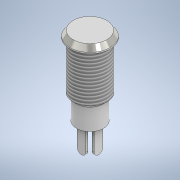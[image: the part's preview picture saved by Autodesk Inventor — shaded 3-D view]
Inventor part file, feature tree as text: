
AUTODESK INVENTOR PART (.ipt)
format: ipt  version: 2021 (Build 250183000, 183)  size: 164,864 bytes
history: native  units: mm
features: extrude x4, sketch x4, chamfer x2, thread x1, fillet x1
ambient origin geometry x8: Origin, YZ Plane, XZ Plane, XY Plane, X Axis, Y Axis, Z Axis, Center Point
bodies: Solid1 (feature_tree)
feature tree (12):
  extrude  "Extrusion1"  Depth=1.5mm TaperAngle=0.0deg
  chamfer  "Chamfer1"  Distance=0.8mm Angle=60.0deg
  extrude  "Extrusion2"  Depth=12.0mm TaperAngle=0.0deg
  chamfer  "Chamfer2"  Distance=0.8mm Angle=60.0deg
  thread  "Thread1"  [1 undecoded]
  extrude  "Extrusion3"  Depth=3.5mm
  extrude  "Extrusion4"  Depth=2.0mm
  fillet  "Fillet1"  Radius=0.5mm
  sketch  "Sketch1"  dims[d0=9.5mm d1=1.5mm d2=0.0mm d3=0.8mm d4=1.2mm d5=60.0deg]
  sketch  "Sketch2"  dims[d6=8.0mm d7=12.0mm d8=0.0mm d9=0.8mm d10=1.2mm d11=60.0deg d12=12.5mm d13=0.0mm]
  sketch  "Sketch3"  dims[d14=5.0mm d15=0.0mm d16=3.5mm]
  sketch  "Sketch4"  dims[d17=3.5mm d18=2.0mm d19=0.5mm d20=0.5mm d21=2.0mm d22=0.5mm d23=2.0mm d24=6.0mm d25=0.0mm d26=1.0mm]
note: 1 required parameter value undecoded (feature->parameter linkage not recoverable at this tier; creation-order binding heuristic only, values carry confidence <= 0.55)
